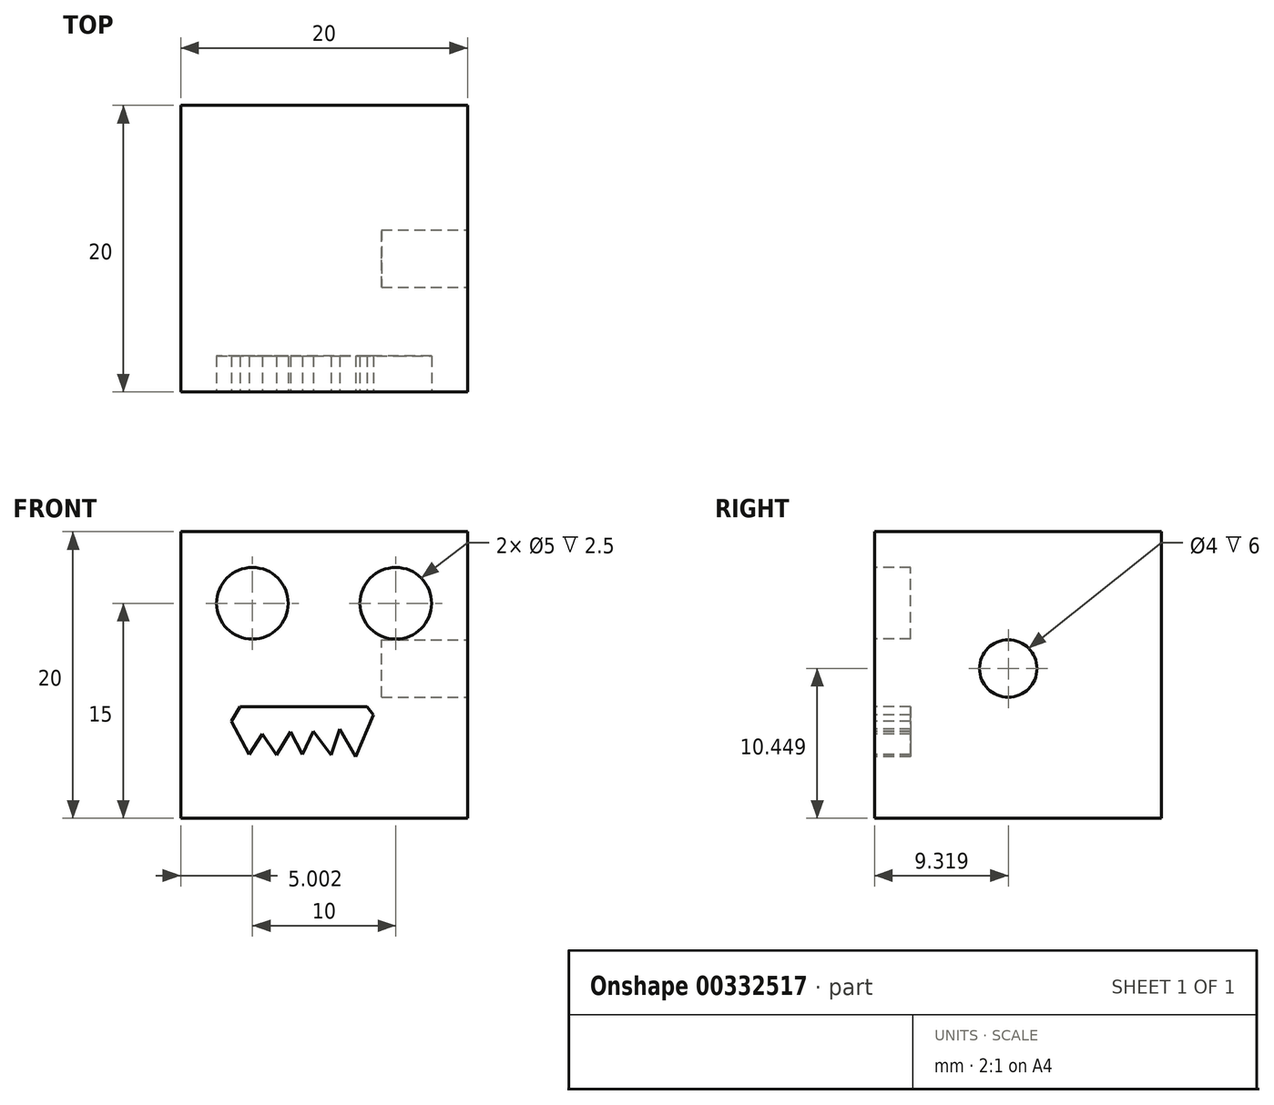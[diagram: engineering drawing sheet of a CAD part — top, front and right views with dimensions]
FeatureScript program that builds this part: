
annotation { "Feature Type Name" : "Feature", "Feature Type Description" : "" }
export const myFeature = defineFeature(function(context is Context, id is Id, definition is map)
    precondition{}
    {
        {
            var Q0;
            Q0=qCreatedBy(makeId("Front.planeOp"),FACE);
            var sketch = newSketch(context, id + "F0", { "sketchPlane" : qUnion([Q0])});
            skLineSegment(sketch, "E0.bottom", {"start": v(-18.58, -0.51) * mm, "end": v(-38.58, -0.51) * mm});
            skLineSegment(sketch, "E0.top", {"start": v(-18.58, 19.49) * mm, "end": v(-38.58, 19.49) * mm});
            skLineSegment(sketch, "E0.left", {"start": v(-18.58, -0.51) * mm, "end": v(-18.58, 19.49) * mm});
            skLineSegment(sketch, "E0.right", {"start": v(-38.58, -0.51) * mm, "end": v(-38.58, 19.49) * mm});
            skPoint(sketch, "E0.middle", {"position": v(-28.58, 9.49) * mm});
            skSolve(sketch);
        }
        {
            var Q0;
            Q0 = qSketchRegion(id + "F0", true);
            extrude(context, id + "F1", {"entities" : qUnion([Q0]), "depth" : 20 * mm});
        }
        {
            var Q0;
            Q0=makeQuery(id+"F1.opExtrude","CAP_FACE",FACE,{"disambiguationData":[OSD([sQuery(id+"F0.wireOp",EDGE,"E0.bottom"),sQuery(id+"F0.wireOp",EDGE,"E0.top"),sQuery(id+"F0.wireOp",EDGE,"E0.left"),sQuery(id+"F0.wireOp",EDGE,"E0.right")])],"isStart":false});
            var sketch = newSketch(context, id + "F2", { "sketchPlane" : qUnion([Q0])});
            skCircle(sketch, "E1", {"center": v(-33.58, 14.49) * mm, "radius": 2.5 * mm});
            skCircle(sketch, "E2", {"center": v(-23.58, 14.49) * mm, "radius": 2.5 * mm});
            skSolve(sketch);
        }
        {
            var Q0;
            Q0=makeQuery(id+"F2.imprint","IMPRINT",FACE,{"disambiguationData":[TD([[makeQuery(id+"F2.imprint","IMPRINT",EDGE,{"derivedFrom":sQuery(id+"F2.wireOp",EDGE,"E1")}),1.0]])]});
            extrude(context, id + "F3", {"entities" : qUnion([Q0]), "operationType" : NewBodyOperationType.REMOVE, "oppositeDirection" : true, "depth" : 2.5 * mm});
        }
        {
            var Q0;
            Q0=makeQuery(id+"F1.opExtrude","CAP_FACE",FACE,{"disambiguationData":[OSD([sQuery(id+"F0.wireOp",EDGE,"E0.bottom"),sQuery(id+"F0.wireOp",EDGE,"E0.top"),sQuery(id+"F0.wireOp",EDGE,"E0.left"),sQuery(id+"F0.wireOp",EDGE,"E0.right")])],"isStart":false});
            var sketch = newSketch(context, id + "F4", { "sketchPlane" : qUnion([Q0])});
            skCircle(sketch, "E3", {"center": v(-23.58, 14.49) * mm, "radius": 2.5 * mm});
            skSolve(sketch);
        }
        {
            var Q0;
            Q0=makeQuery(id+"F4.imprint","IMPRINT",FACE,{"disambiguationData":[TD([[makeQuery(id+"F4.imprint","IMPRINT",EDGE,{"derivedFrom":sQuery(id+"F4.wireOp",EDGE,"E3")}),1.0]])]});
            var Q1;
            Q1=sQuery(id+"F4.wireOp",EDGE,"E3");
            extrude(context, id + "F5", {"entities" : qUnion([Q0]), "operationType" : NewBodyOperationType.REMOVE, "surfaceEntities" : qUnion([Q1]), "oppositeDirection" : true, "depth" : 2.5 * mm});
        }
        {
            var Q0;
            Q0=makeQuery(id+"F1.opExtrude","CAP_FACE",FACE,{"disambiguationData":[OSD([sQuery(id+"F0.wireOp",EDGE,"E0.bottom"),sQuery(id+"F0.wireOp",EDGE,"E0.top"),sQuery(id+"F0.wireOp",EDGE,"E0.left"),sQuery(id+"F0.wireOp",EDGE,"E0.right")])],"isStart":false});
            var sketch = newSketch(context, id + "F6", { "sketchPlane" : qUnion([Q0])});
            skLineSegment(sketch, "E4", {"start": v(-35.03, 6.26) * mm, "end": v(-33.8, 3.96) * mm});
            skLineSegment(sketch, "E5", {"start": v(-33.8, 3.96) * mm, "end": v(-32.88, 5.38) * mm});
            skLineSegment(sketch, "E6", {"start": v(-32.88, 5.38) * mm, "end": v(-31.9, 3.92) * mm});
            skLineSegment(sketch, "E7", {"start": v(-31.9, 3.92) * mm, "end": v(-30.92, 5.54) * mm});
            skLineSegment(sketch, "E8", {"start": v(-30.92, 5.54) * mm, "end": v(-30.1, 3.96) * mm});
            skLineSegment(sketch, "E9", {"start": v(-30.1, 3.96) * mm, "end": v(-29.34, 5.57) * mm});
            skLineSegment(sketch, "E10", {"start": v(-29.34, 5.57) * mm, "end": v(-28.1, 3.92) * mm});
            skLineSegment(sketch, "E11", {"start": v(-28.1, 3.92) * mm, "end": v(-27.47, 5.73) * mm});
            skLineSegment(sketch, "E12", {"start": v(-27.47, 5.73) * mm, "end": v(-26.36, 3.77) * mm});
            skLineSegment(sketch, "E13", {"start": v(-26.36, 3.77) * mm, "end": v(-25.13, 6.7) * mm});
            skLineSegment(sketch, "E14", {"start": v(-25.13, 6.7) * mm, "end": v(-25.57, 7.28) * mm});
            skLineSegment(sketch, "E15", {"start": v(-25.57, 7.28) * mm, "end": v(-34.43, 7.28) * mm});
            skLineSegment(sketch, "E16", {"start": v(-34.43, 7.28) * mm, "end": v(-35.03, 6.26) * mm});
            skSolve(sketch);
        }
        {
            var Q0;
            Q0 = qSketchRegion(id + "F6", true);
            extrude(context, id + "F7", {"entities" : qUnion([Q0]), "operationType" : NewBodyOperationType.REMOVE, "oppositeDirection" : true, "depth" : 2.5 * mm});
        }
        {
            var Q0;
            Q0=makeQuery(id+"F1.opExtrude","SWEPT_FACE",FACE,{"disambiguationData":[OSD([sQuery(id+"F0.wireOp",EDGE,"E0.left")])]});
            var sketch = newSketch(context, id + "F8", { "sketchPlane" : qUnion([Q0])});
            skCircle(sketch, "E17", {"center": v(-10.68, 9.94) * mm, "radius": 2 * mm});
            skSolve(sketch);
        }
        {
            var Q0;
            Q0 = qSketchRegion(id + "F8", true);
            extrude(context, id + "F9", {"entities" : qUnion([Q0]), "operationType" : NewBodyOperationType.REMOVE, "oppositeDirection" : true, "depth" : 6 * mm});
        }
    });
